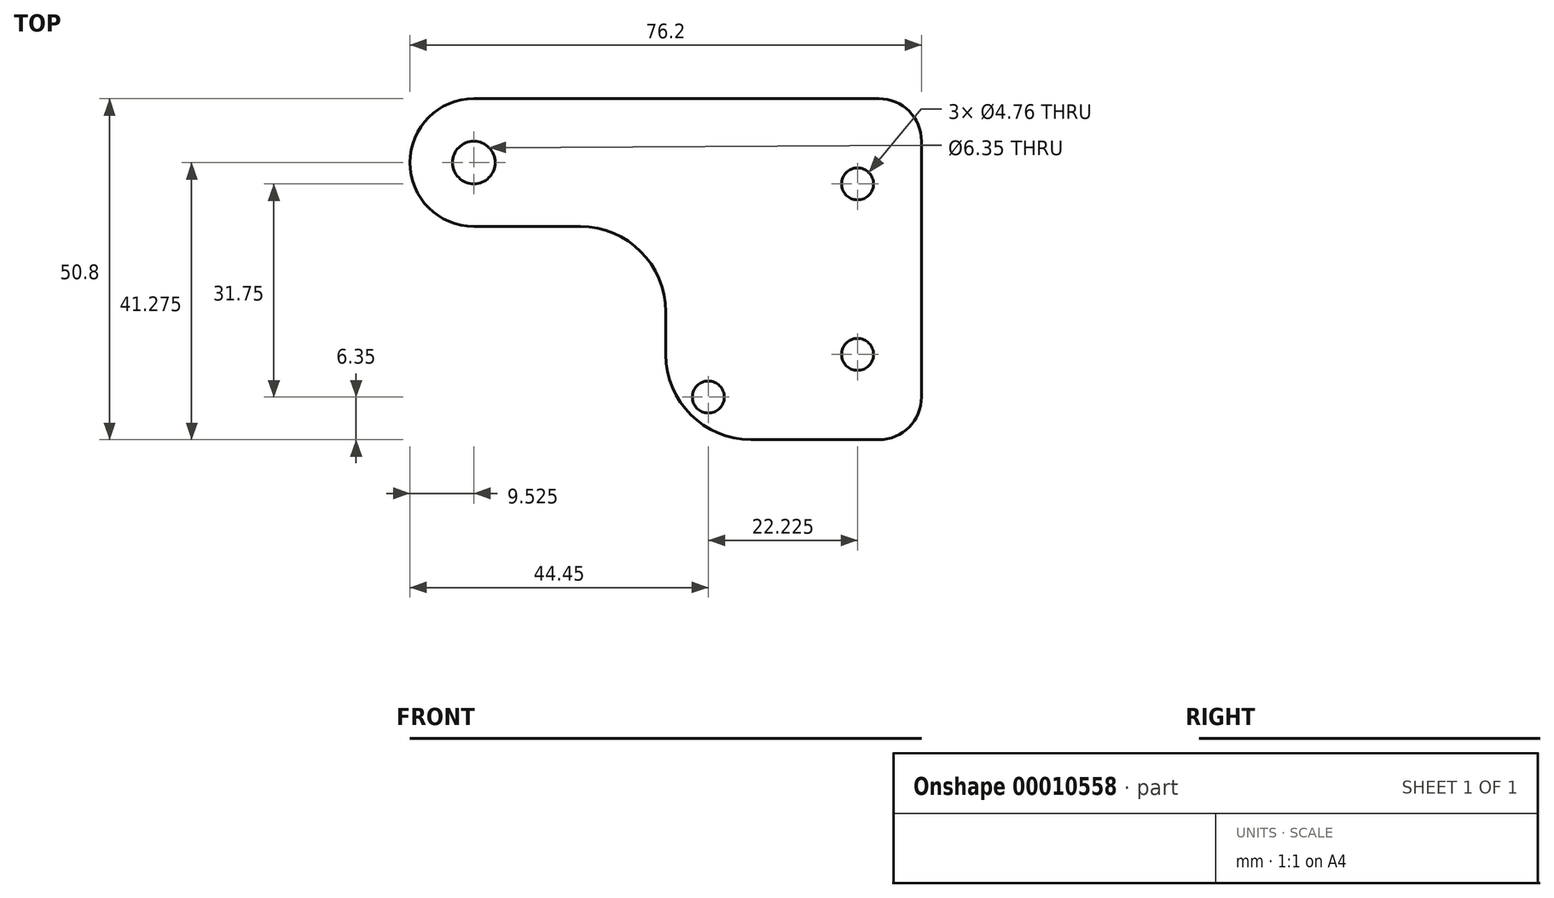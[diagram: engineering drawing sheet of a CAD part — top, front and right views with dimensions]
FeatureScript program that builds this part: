
annotation { "Feature Type Name" : "Feature", "Feature Type Description" : "" }
export const myFeature = defineFeature(function(context is Context, id is Id, definition is map)
    precondition{}
    {
        {
            var Q0;
            Q0=qCreatedBy(makeId("Top.planeOp"),FACE);
            var sketch = newSketch(context, id + "F0", { "sketchPlane" : qUnion([Q0])});
            skLineSegment(sketch, "E0.top", {"start": v(0, 50.8) * mm, "end": v(76.2, 50.8) * mm});
            skLineSegment(sketch, "E0.right", {"start": v(76.2, 0) * mm, "end": v(76.2, 50.8) * mm});
            skLineSegment(sketch, "E1", {"start": v(90.83, 41.28) * mm, "end": v(-19.13, 41.27) * mm, "construction": true});
            skLineSegment(sketch, "E2", {"start": v(-7.71, 6.35) * mm, "end": v(87.62, 6.35) * mm, "construction": true});
            skLineSegment(sketch, "E3", {"start": v(-9.16, 12.7) * mm, "end": v(88.42, 12.7) * mm, "construction": true});
            skLineSegment(sketch, "E4", {"start": v(-11.25, 38.1) * mm, "end": v(88.58, 38.1) * mm, "construction": true});
            skLineSegment(sketch, "E5", {"start": v(44.45, -13.84) * mm, "end": v(44.45, 58.94) * mm, "construction": true});
            skLineSegment(sketch, "E6", {"start": v(66.68, 58.94) * mm, "end": v(66.68, -14.6) * mm, "construction": true});
            skLineSegment(sketch, "E7", {"start": v(38.1, 31.75) * mm, "end": v(0, 31.75) * mm});
            skLineSegment(sketch, "E8.bottom", {"start": v(0, 31.75) * mm, "end": v(38.1, 31.75) * mm});
            skLineSegment(sketch, "E8.right", {"start": v(38.1, 31.75) * mm, "end": v(38.1, 0) * mm});
            skLineSegment(sketch, "E9", {"start": v(0, 31.75) * mm, "end": v(0, 50.8) * mm});
            skLineSegment(sketch, "E10", {"start": v(38.1, 0) * mm, "end": v(76.2, 0) * mm});
            skCircle(sketch, "E11", {"center": v(44.45, 6.35) * mm, "radius": 2.38 * mm});
            skCircle(sketch, "E12", {"center": v(66.68, 12.7) * mm, "radius": 2.38 * mm});
            skCircle(sketch, "E13", {"center": v(66.68, 38.1) * mm, "radius": 2.38 * mm});
            skCircle(sketch, "E14", {"center": v(9.53, 41.27) * mm, "radius": 3.18 * mm});
            skSolve(sketch);
        }
        {
            var Q0;
            Q0=makeQuery(id+"F0.imprint","IMPRINT",FACE,{"disambiguationData":[TD([[makeQuery(id+"F0.imprint","IMPRINT",EDGE,{"derivedFrom":sQuery(id+"F0.wireOp",EDGE,"E0.top")}),-1.0]])]});
            extrude(context, id + "F1", {"entities" : qUnion([Q0]), "depth" : 1 / 203.2 * mm});
        }
        {
            var Q0;
            Q0=makeQuery(id+"F1.opExtrude","SWEPT_EDGE",EDGE,{"disambiguationData":[OSD([sQuery(id+"F0.wireOp",EDGE,"E8.bottom"),sQuery(id+"F0.wireOp",EDGE,"E9")])]});
            var Q1;
            Q1=makeQuery(id+"F1.opExtrude","SWEPT_EDGE",EDGE,{"disambiguationData":[OSD([sQuery(id+"F0.wireOp",EDGE,"E0.top"),sQuery(id+"F0.wireOp",EDGE,"E9")])]});
            fillet(context, id + "F2", {"entities" : qUnion([Q0, Q1]), "radius" : 9.52 * mm, "tangentPropagation" : true, "allowEdgeOverflow" : false});
        }
        {
            var Q0;
            Q0=makeQuery(id+"F1.opExtrude","SWEPT_EDGE",EDGE,{"disambiguationData":[OSD([sQuery(id+"F0.wireOp",EDGE,"E8.bottom"),sQuery(id+"F0.wireOp",EDGE,"E8.right")])]});
            fillet(context, id + "F3", {"entities" : qUnion([Q0]), "radius" : 12.7 * mm, "tangentPropagation" : true, "allowEdgeOverflow" : false});
        }
        {
            var Q0;
            Q0=makeQuery(id+"F1.opExtrude","SWEPT_EDGE",EDGE,{"disambiguationData":[OSD([sQuery(id+"F0.wireOp",EDGE,"E8.right"),sQuery(id+"F0.wireOp",EDGE,"E10")])]});
            var Q1;
            Q1=makeQuery(id+"F1.opExtrude","SWEPT_EDGE",EDGE,{"disambiguationData":[OSD([sQuery(id+"F0.wireOp",EDGE,"E0.right"),sQuery(id+"F0.wireOp",EDGE,"E10")])]});
            var Q2;
            Q2=makeQuery(id+"F1.opExtrude","SWEPT_EDGE",EDGE,{"disambiguationData":[OSD([sQuery(id+"F0.wireOp",EDGE,"E0.top"),sQuery(id+"F0.wireOp",EDGE,"E0.right")])]});
            fillet(context, id + "F4", {"entities" : qUnion([Q0, Q1, Q2]), "radius" : 6.35 * mm, "tangentPropagation" : true, "allowEdgeOverflow" : false});
        }
    });
